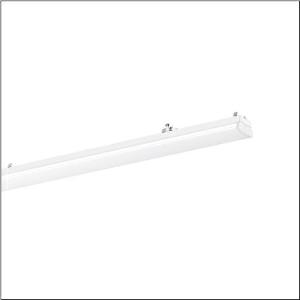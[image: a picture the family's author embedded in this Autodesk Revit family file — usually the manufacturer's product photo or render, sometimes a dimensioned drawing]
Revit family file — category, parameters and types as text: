
# Revit family: licross_r__11_recessed_opal_mo_51tl1ddn46xg_c64a
name_source: partatom
category: Lighting Fixtures
units: mm (PartAtom-declared; Revit-internal decimal feet)

## family parameters
Cut with Voids When Loaded = No
Host = Face
Light Source = No
Part Type = Normal
Room Calculation Point = No
Round Connector Dimension = Use Diameter
Shared = No

## types (1)
- --- (1 x LED, 6320 lm, 35.2 W, 4000K)
    Apparent Load = 35 VA
    CIE Flux Codes = 44 73 91 87 100
    Color Rendering = 80
    Color Temperature = 4000K
    Default Elevation = 1800 mm
    Description = Licross® 11 recessed opal MO, luminaire insert, of sheet steel, coil coated, white, length: 1.500mm, width: 76mm, height: 87mm, LED rated luminous flux: 6.320lm, light colour: 840, control gear: DALI 2, with plug, 5-pole, with phase selection, mains connection: 220..240V, AC, 50/60Hz, rated input power: 35W, halogen-free wiring, primary optical cover: cover, of PMMA, light emission: direct with ceiling illumination distribution, primary light characteristic: symmetric, protection rating (complete): IP40, insulation class (complete): insulation class I (protective earthing), certification: CE, ENEC, VDE, UKCA, protection symbol: D if used in an environment without relevant dust loads with corresponding accessories, impact resistance: IK06, permissible ambient temperature for indoor applications: -25..+40°C, corresponds to IFS (International Featured Standards) requirements for safety and quality in the food industry, reducing of maximum allowable ambient temperature of 5°C with ceiling mounting, LABS conformity tested according to VDMA 24364:2018-05, packaging unit: 1 piece
    Height = 83 mm
    Lamp = 1 x LED
    Lamp Light Flux = 6320 lm
    Lamp Power = 35.2 W
    Lamp count = 1
    Length = 1500 mm
    Luminous efficacy = 180 lm/W
    Manufacturer = Siteco
    ModVariant = No
    Model = 51TL1DDN46XG
    Mounting Place = Ceiling
    Mounting Type = Pendant
    Number of Poles = 1
    OnlyDefault = Yes
    Power Factor = 1
    Product Name = Licross® 11 recessed opal MO
    Product group = luminaire insert
    ProductGroupID = 901
    Protection Class = Protection class I
    Protection Degree = IP 40
    RLX_Detail_Level = 1
    RLX_Emergency_Light_Flux = 0 lm
    RLX_Emergency_Type = 0
    RLX_Emergency_Type_DB = No
    RlxData = <blob elided: 18001 chars, md5=69edf81d>
    Socket = socket
    Standby Power = 0 W
    System Light Flux = 6320 lm
    System Power = 35 W
    Type Comments = factory setting: luminous flux: 100 % | dim-lin: 254 | 238 mA
    Type Image = l_1313666.jpg
    URL = http://relux.com
    VarID = @adj_027431
    Voltage = 0 V
    Weight = 0.00 kg
    Width = 76 mm

## geometry (parser evidence)
native form markers: Blend x4, Sweep x14
no freeform markers — native parametric forms only
